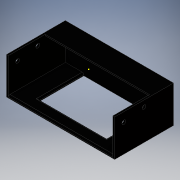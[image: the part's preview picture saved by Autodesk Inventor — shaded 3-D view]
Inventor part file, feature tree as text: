
AUTODESK INVENTOR PART (.ipt)
format: ipt  version: 2016 (Build 200138000, 138)  size: 205,312 bytes
history: native  units: in
note: dims shown in document units (in); Inventor stores cm internally (conversion verified against a paired STEP export)
features: sketch x10, extrude x7, fillet x4, hole x2, projected_geometry x1
ambient origin geometry x8: Origin, YZ Plane, XZ Plane, XY Plane, X Axis, Y Axis, Z Axis, Center Point
bodies: Solid1 (feature_tree)
feature tree (24):
  sketch  "Sketch1"  dims[d0=5.0in d1=8.8189in]
  extrude  "Extrusion1"  Depth=8.8189in
  extrude  "Extrusion2"  Depth=3.0in
  extrude  "Extrusion3"  Depth=2.9in TaperAngle=0.0deg
  extrude  "Extrusion4"  Depth=1.5in TaperAngle=0.0deg
  extrude  "Extrusion5"  Depth=0.2in
  extrude  "Extrusion6"  Depth=0.2in TaperAngle=0.0deg
  extrude  "Extrusion7"  Depth=5.5in TaperAngle=0.0deg
  fillet  "Fillet1"  Radius=3.0in
  fillet  "Fillet2"  Radius=0.125in
  fillet  "Fillet3"  Radius=0.125in
  hole  "Hole1"  [1 undecoded]
  fillet  "Fillet4"  Radius=0.125in
  hole  "Hole2"  [1 undecoded]
  sketch  "Sketch2"  dims[d2=3.0in d3=0.0in d4=4.7in]
  sketch  "Sketch3"  dims[d5=8.5in d6=2.9in d7=0.0in]
  sketch  "Sketch4"  dims[d8=0.2in d9=1.5in d10=0.0in]
  sketch  "Sketch5"  dims[d11=4.7in d12=0.2in]
  sketch  "Sketch7"  dims[d13=1.5in d14=0.0in d15=0.2in d16=0.0in]
  projected_geometry  "Projected Loop1"
  sketch  "Sketch8"  dims[d17=1.0in d18=5.5in d19=0.0in d20=3.0in d21=0.0in d22=0.125in d23=0.125in]
  sketch  "Sketch9"  dims[d24=0.125in d27=0.315in]
  sketch  "Sketch10"  dims[d28=0.315in d29=0.75in d30=0.375in d31=0.25in d32=0.5635in d33=1.0in d34=0.8108in d35=0.125in]
  sketch  "Sketch11"  dims[d37=0.315in d38=0.75in d39=0.375in d40=0.25in d41=0.5635in d42=1.0in d43=0.8108in]
note: 2 required parameter values undecoded (feature->parameter linkage not recoverable at this tier; creation-order binding heuristic only, values carry confidence <= 0.55)
